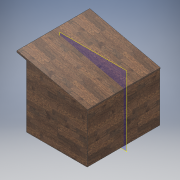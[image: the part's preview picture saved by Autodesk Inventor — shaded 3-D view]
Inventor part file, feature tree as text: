
AUTODESK INVENTOR PART (.ipt)
format: ipt  version: 2017 (Build 210142000, 142)  size: 346,624 bytes
history: native  units: in
note: dims shown in document units (in); Inventor stores cm internally (conversion verified against a paired STEP export)
features: extrude x12, sketch x12, projected_geometry x10, plane x1, mirror x1
ambient origin geometry x8: Origin, YZ Plane, XZ Plane, XY Plane, X Axis, Y Axis, Z Axis, Center Point
bodies: Solid1 (feature_tree)
feature tree (36):
  extrude  "Extrusion1"  Depth=36.0in
  extrude  "Extrusion5"  Depth=0.75in
  extrude  "Extrusion7"  Depth=0.75in
  extrude  "Extrusion8"  TaperAngle=90.0deg  [1 undecoded]
  plane  "Work Plane2"
  mirror  "Mirror1"
  extrude  "Extrusion9"  Depth=24.0in TaperAngle=0.0deg
  extrude  "Extrusion10"  Depth=0.75in
  extrude  "Extrusion11"  Depth=18.0in TaperAngle=0.0deg
  extrude  "Extrusion12"  Depth=0.75in TaperAngle=0.0deg
  extrude  "Extrusion13"  Depth=0.75in
  extrude  "Extrusion14"  Depth=0.75in
  extrude  "Extrusion15"  Depth=5.0in TaperAngle=0.0deg
  extrude  "Extrusion16"  Depth=5.0in TaperAngle=0.0deg
  sketch  "Sketch1"  dims[d0=30.0in d1=36.0in]
  sketch  "Sketch5"  dims[d2=0.75in d3=0.0in d22=6.0in]
  projected_geometry  "Projected Loop4"
  sketch  "Sketch7"  dims[d23=0.0871in d25=0.75in]
  projected_geometry  "Projected Loop7"
  sketch  "Sketch8"  dims[d26=90.0deg d28=90.0deg]
  projected_geometry  "Projected Loop8"
  sketch  "Sketch9"  dims[d29=90.0deg d30=24.0in d31=0.0in]
  projected_geometry  "Projected Loop9"
  sketch  "Sketch12"  dims[d38=0.75in d39=0.75in]
  projected_geometry  "Projected Loop13"
  sketch  "Sketch13"  dims[d40=18.0in d41=24.0in d42=0.0in]
  projected_geometry  "Projected Loop14"
  sketch  "Sketch14"  dims[d43=0.75in d44=0.0in d45=0.75in d46=0.0in]
  projected_geometry  "Projected Loop15"
  sketch  "Sketch15"  dims[d57=0.75in d58=6.0in]
  projected_geometry  "Projected Loop16"
  sketch  "Sketch16"  dims[d59=1.0in d60=0.0in d61=0.75in]
  projected_geometry  "Projected Loop17"
  sketch  "Sketch17"  dims[d62=1.0in d63=0.0in d64=5.0in d65=0.0in]
  sketch  "Sketch18"  dims[d66=0.75in d67=5.0in d68=0.0in d69=0.75in d70=5.0in d71=0.75in d72=5.0in d73=5.0in d74=0.0in d75=0.75in d76=5.0in d77=0.0in d78=0.5in d79=0.0in]
  projected_geometry  "Projected Loop18"
note: 1 required parameter value undecoded (feature->parameter linkage not recoverable at this tier; creation-order binding heuristic only, values carry confidence <= 0.55)
